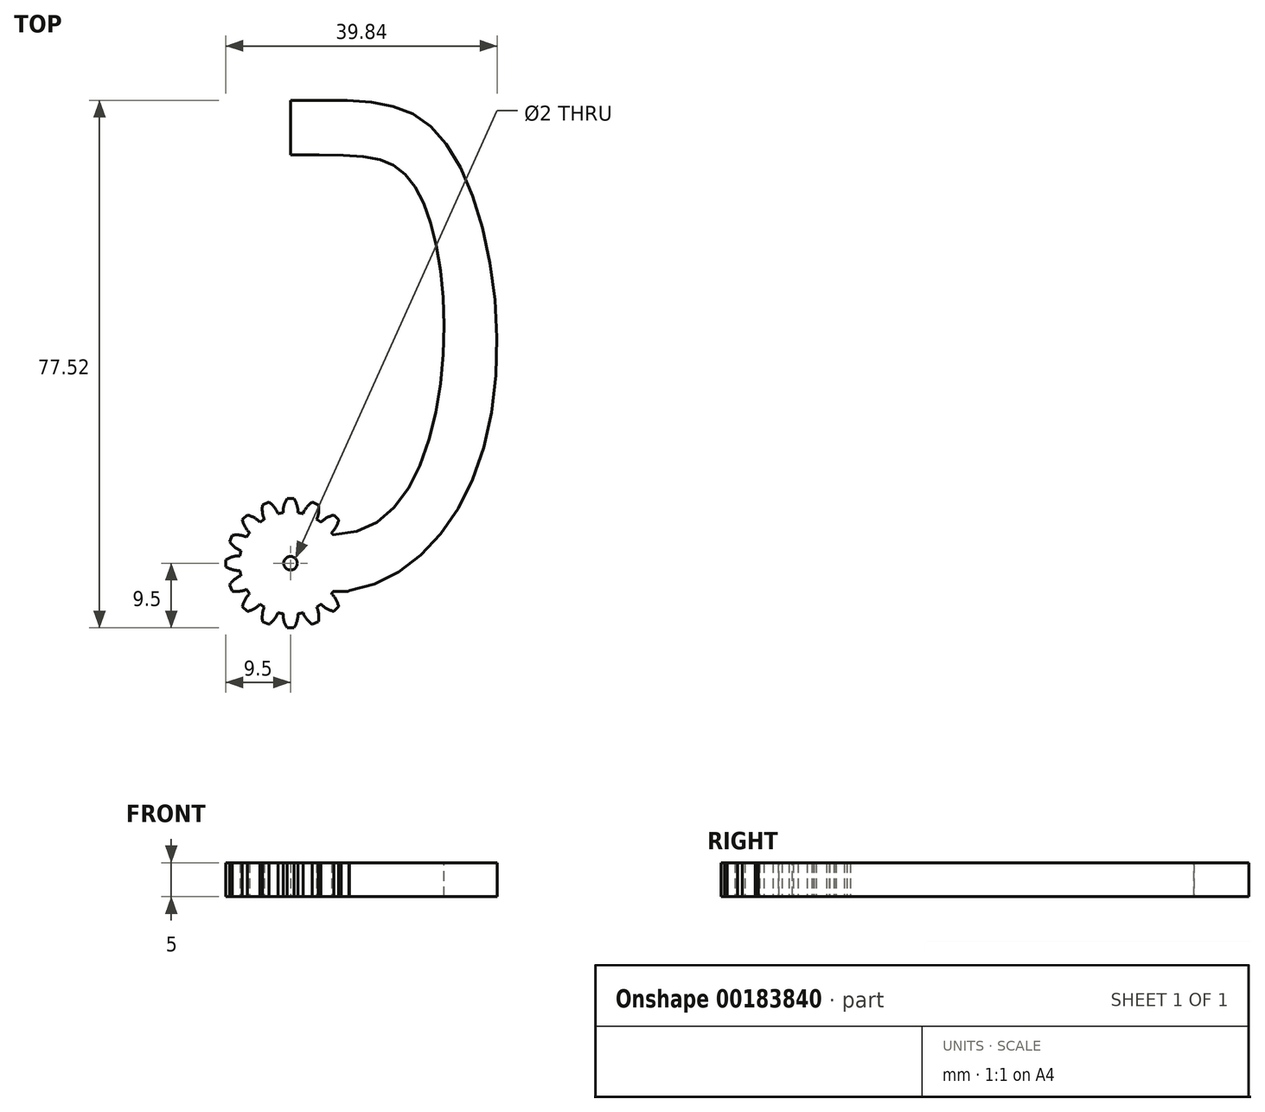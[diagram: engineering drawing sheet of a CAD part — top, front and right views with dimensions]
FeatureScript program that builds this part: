
annotation { "Feature Type Name" : "Feature", "Feature Type Description" : "" }
export const myFeature = defineFeature(function(context is Context, id is Id, definition is map)
    precondition{}
    {
        {
            var Q0;
            Q0=qCreatedBy(makeId("Top.planeOp"),FACE);
            var sketch = newSketch(context, id + "F0", { "sketchPlane" : qUnion([Q0])});
            skCircle(sketch, "E0", {"center": v(0, 0) * mm, "radius": 7.5 * mm});
            skLineSegment(sketch, "E1", {"start": v(0, 0) * mm, "end": v(0, 7.5) * mm, "construction": true});
            skLineSegment(sketch, "E2", {"start": v(0, 9.5) * mm, "end": v(-0.5, 9.5) * mm});
            skArc(sketch, "E3", {"start": v(-0.5, 9.5) * mm, "mid": v(-0.95, 8.5) * mm, "end": v(-1.09, 7.42) * mm});
            skLineSegment(sketch, "E4.MirrorCS", {"start": v(0, 9.5) * mm, "end": v(0.5, 9.5) * mm});
            skArc(sketch, "E5.MirrorCS", {"start": v(0.5, 9.5) * mm, "mid": v(0.95, 8.5) * mm, "end": v(1.09, 7.42) * mm});
            skArc(sketch, "E6.1.0", {"start": v(-4.1, 8.59) * mm, "mid": v(-4.13, 7.5) * mm, "end": v(-3.85, 6.44) * mm});
            skLineSegment(sketch, "E6.1.1", {"start": v(-3.64, 8.78) * mm, "end": v(-4.1, 8.59) * mm});
            skLineSegment(sketch, "E6.1.2", {"start": v(-3.64, 8.78) * mm, "end": v(-3.17, 8.97) * mm});
            skArc(sketch, "E6.1.3", {"start": v(-3.17, 8.97) * mm, "mid": v(-2.38, 8.22) * mm, "end": v(-1.83, 7.27) * mm});
            skArc(sketch, "E6.2.0", {"start": v(-7.07, 6.36) * mm, "mid": v(-6.69, 5.34) * mm, "end": v(-6.02, 4.48) * mm});
            skLineSegment(sketch, "E6.2.1", {"start": v(-6.72, 6.72) * mm, "end": v(-7.07, 6.36) * mm});
            skLineSegment(sketch, "E6.2.2", {"start": v(-6.72, 6.72) * mm, "end": v(-6.36, 7.07) * mm});
            skArc(sketch, "E6.2.3", {"start": v(-6.36, 7.07) * mm, "mid": v(-5.34, 6.69) * mm, "end": v(-4.48, 6.02) * mm});
            skArc(sketch, "E6.3.0", {"start": v(-8.97, 3.17) * mm, "mid": v(-8.22, 2.38) * mm, "end": v(-7.27, 1.83) * mm});
            skLineSegment(sketch, "E6.3.1", {"start": v(-8.78, 3.64) * mm, "end": v(-8.97, 3.17) * mm});
            skLineSegment(sketch, "E6.3.2", {"start": v(-8.78, 3.64) * mm, "end": v(-8.59, 4.1) * mm});
            skArc(sketch, "E6.3.3", {"start": v(-8.59, 4.1) * mm, "mid": v(-7.5, 4.13) * mm, "end": v(-6.44, 3.85) * mm});
            skArc(sketch, "E6.4.0", {"start": v(-9.5, -0.5) * mm, "mid": v(-8.5, -0.95) * mm, "end": v(-7.42, -1.09) * mm});
            skLineSegment(sketch, "E6.4.1", {"start": v(-9.5, 0) * mm, "end": v(-9.5, -0.5) * mm});
            skLineSegment(sketch, "E6.4.2", {"start": v(-9.5, 0) * mm, "end": v(-9.5, 0.5) * mm});
            skArc(sketch, "E6.4.3", {"start": v(-9.5, 0.5) * mm, "mid": v(-8.5, 0.95) * mm, "end": v(-7.42, 1.09) * mm});
            skArc(sketch, "E6.5.0", {"start": v(-8.59, -4.1) * mm, "mid": v(-7.5, -4.13) * mm, "end": v(-6.44, -3.85) * mm});
            skLineSegment(sketch, "E6.5.1", {"start": v(-8.78, -3.64) * mm, "end": v(-8.59, -4.1) * mm});
            skLineSegment(sketch, "E6.5.2", {"start": v(-8.78, -3.64) * mm, "end": v(-8.97, -3.17) * mm});
            skArc(sketch, "E6.5.3", {"start": v(-8.97, -3.17) * mm, "mid": v(-8.22, -2.38) * mm, "end": v(-7.27, -1.83) * mm});
            skArc(sketch, "E6.6.0", {"start": v(-6.36, -7.07) * mm, "mid": v(-5.34, -6.69) * mm, "end": v(-4.48, -6.02) * mm});
            skLineSegment(sketch, "E6.6.1", {"start": v(-6.72, -6.72) * mm, "end": v(-6.36, -7.07) * mm});
            skLineSegment(sketch, "E6.6.2", {"start": v(-6.72, -6.72) * mm, "end": v(-7.07, -6.36) * mm});
            skArc(sketch, "E6.6.3", {"start": v(-7.07, -6.36) * mm, "mid": v(-6.69, -5.34) * mm, "end": v(-6.02, -4.48) * mm});
            skArc(sketch, "E6.7.0", {"start": v(-3.17, -8.97) * mm, "mid": v(-2.38, -8.22) * mm, "end": v(-1.83, -7.27) * mm});
            skLineSegment(sketch, "E6.7.1", {"start": v(-3.64, -8.78) * mm, "end": v(-3.17, -8.97) * mm});
            skLineSegment(sketch, "E6.7.2", {"start": v(-3.64, -8.78) * mm, "end": v(-4.1, -8.59) * mm});
            skArc(sketch, "E6.7.3", {"start": v(-4.1, -8.59) * mm, "mid": v(-4.13, -7.5) * mm, "end": v(-3.85, -6.44) * mm});
            skArc(sketch, "E6.8.0", {"start": v(0.5, -9.5) * mm, "mid": v(0.95, -8.5) * mm, "end": v(1.09, -7.42) * mm});
            skLineSegment(sketch, "E6.8.1", {"start": v(0, -9.5) * mm, "end": v(0.5, -9.5) * mm});
            skLineSegment(sketch, "E6.8.2", {"start": v(0, -9.5) * mm, "end": v(-0.5, -9.5) * mm});
            skArc(sketch, "E6.8.3", {"start": v(-0.5, -9.5) * mm, "mid": v(-0.95, -8.5) * mm, "end": v(-1.09, -7.42) * mm});
            skArc(sketch, "E6.9.0", {"start": v(4.1, -8.59) * mm, "mid": v(4.13, -7.5) * mm, "end": v(3.85, -6.44) * mm});
            skLineSegment(sketch, "E6.9.1", {"start": v(3.64, -8.78) * mm, "end": v(4.1, -8.59) * mm});
            skLineSegment(sketch, "E6.9.2", {"start": v(3.64, -8.78) * mm, "end": v(3.17, -8.97) * mm});
            skArc(sketch, "E6.9.3", {"start": v(3.17, -8.97) * mm, "mid": v(2.38, -8.22) * mm, "end": v(1.83, -7.27) * mm});
            skArc(sketch, "E6.10.0", {"start": v(7.07, -6.36) * mm, "mid": v(6.69, -5.34) * mm, "end": v(6.02, -4.48) * mm});
            skLineSegment(sketch, "E6.10.1", {"start": v(6.72, -6.72) * mm, "end": v(7.07, -6.36) * mm});
            skLineSegment(sketch, "E6.10.2", {"start": v(6.72, -6.72) * mm, "end": v(6.36, -7.07) * mm});
            skArc(sketch, "E6.10.3", {"start": v(6.36, -7.07) * mm, "mid": v(5.34, -6.69) * mm, "end": v(4.48, -6.02) * mm});
            skArc(sketch, "E6.11.0", {"start": v(8.97, -3.17) * mm, "mid": v(8.22, -2.38) * mm, "end": v(7.27, -1.83) * mm});
            skLineSegment(sketch, "E6.11.1", {"start": v(8.78, -3.64) * mm, "end": v(8.97, -3.17) * mm});
            skLineSegment(sketch, "E6.11.2", {"start": v(8.78, -3.64) * mm, "end": v(8.59, -4.1) * mm});
            skArc(sketch, "E6.11.3", {"start": v(8.59, -4.1) * mm, "mid": v(7.5, -4.13) * mm, "end": v(6.44, -3.85) * mm});
            skArc(sketch, "E6.12.0", {"start": v(9.5, 0.5) * mm, "mid": v(8.5, 0.95) * mm, "end": v(7.42, 1.09) * mm});
            skLineSegment(sketch, "E6.12.1", {"start": v(9.5, 0) * mm, "end": v(9.5, 0.5) * mm});
            skLineSegment(sketch, "E6.12.2", {"start": v(9.5, 0) * mm, "end": v(9.5, -0.5) * mm});
            skArc(sketch, "E6.12.3", {"start": v(9.5, -0.5) * mm, "mid": v(8.5, -0.95) * mm, "end": v(7.42, -1.09) * mm});
            skArc(sketch, "E6.13.0", {"start": v(8.59, 4.1) * mm, "mid": v(7.5, 4.13) * mm, "end": v(6.44, 3.85) * mm});
            skLineSegment(sketch, "E6.13.1", {"start": v(8.78, 3.64) * mm, "end": v(8.59, 4.1) * mm});
            skLineSegment(sketch, "E6.13.2", {"start": v(8.78, 3.64) * mm, "end": v(8.97, 3.17) * mm});
            skArc(sketch, "E6.13.3", {"start": v(8.97, 3.17) * mm, "mid": v(8.22, 2.38) * mm, "end": v(7.27, 1.83) * mm});
            skArc(sketch, "E6.14.0", {"start": v(6.36, 7.07) * mm, "mid": v(5.34, 6.69) * mm, "end": v(4.48, 6.02) * mm});
            skLineSegment(sketch, "E6.14.1", {"start": v(6.72, 6.72) * mm, "end": v(6.36, 7.07) * mm});
            skLineSegment(sketch, "E6.14.2", {"start": v(6.72, 6.72) * mm, "end": v(7.07, 6.36) * mm});
            skArc(sketch, "E6.14.3", {"start": v(7.07, 6.36) * mm, "mid": v(6.69, 5.34) * mm, "end": v(6.02, 4.48) * mm});
            skArc(sketch, "E6.15.0", {"start": v(3.17, 8.97) * mm, "mid": v(2.38, 8.22) * mm, "end": v(1.83, 7.27) * mm});
            skLineSegment(sketch, "E6.15.1", {"start": v(3.64, 8.78) * mm, "end": v(3.17, 8.97) * mm});
            skLineSegment(sketch, "E6.15.2", {"start": v(3.64, 8.78) * mm, "end": v(4.1, 8.59) * mm});
            skArc(sketch, "E6.15.3", {"start": v(4.1, 8.59) * mm, "mid": v(4.13, 7.5) * mm, "end": v(3.85, 6.44) * mm});
            skSolve(sketch);
        }
        {
            var Q0;
            Q0=qSketchRegion(id+"F0",true);
            extrude(context, id + "F1", {"entities" : qUnion([Q0]), "depth" : 5 * mm});
        }
        {
            var Q0;
            Q0=makeQuery(id+"F1.opExtrude","CAP_FACE",FACE,{"disambiguationData":[OSD([sQuery(id+"F0.wireOp",EDGE,"E0"),sQuery(id+"F0.wireOp",EDGE,"E2"),sQuery(id+"F0.wireOp",EDGE,"E3"),sQuery(id+"F0.wireOp",EDGE,"E4.MirrorCS"),sQuery(id+"F0.wireOp",EDGE,"E5.MirrorCS"),sQuery(id+"F0.wireOp",EDGE,"E6.1.0"),sQuery(id+"F0.wireOp",EDGE,"E6.1.1"),sQuery(id+"F0.wireOp",EDGE,"E6.1.2"),sQuery(id+"F0.wireOp",EDGE,"E6.1.3"),sQuery(id+"F0.wireOp",EDGE,"E6.2.0"),sQuery(id+"F0.wireOp",EDGE,"E6.2.1"),sQuery(id+"F0.wireOp",EDGE,"E6.2.2"),sQuery(id+"F0.wireOp",EDGE,"E6.2.3"),sQuery(id+"F0.wireOp",EDGE,"E6.3.0"),sQuery(id+"F0.wireOp",EDGE,"E6.3.1"),sQuery(id+"F0.wireOp",EDGE,"E6.3.2"),sQuery(id+"F0.wireOp",EDGE,"E6.3.3"),sQuery(id+"F0.wireOp",EDGE,"E6.4.0"),sQuery(id+"F0.wireOp",EDGE,"E6.4.1"),sQuery(id+"F0.wireOp",EDGE,"E6.4.2"),sQuery(id+"F0.wireOp",EDGE,"E6.4.3"),sQuery(id+"F0.wireOp",EDGE,"E6.5.0"),sQuery(id+"F0.wireOp",EDGE,"E6.5.1"),sQuery(id+"F0.wireOp",EDGE,"E6.5.2"),sQuery(id+"F0.wireOp",EDGE,"E6.5.3"),sQuery(id+"F0.wireOp",EDGE,"E6.6.0"),sQuery(id+"F0.wireOp",EDGE,"E6.6.1"),sQuery(id+"F0.wireOp",EDGE,"E6.6.2"),sQuery(id+"F0.wireOp",EDGE,"E6.6.3"),sQuery(id+"F0.wireOp",EDGE,"E6.7.0"),sQuery(id+"F0.wireOp",EDGE,"E6.7.1"),sQuery(id+"F0.wireOp",EDGE,"E6.7.2"),sQuery(id+"F0.wireOp",EDGE,"E6.7.3"),sQuery(id+"F0.wireOp",EDGE,"E6.8.0"),sQuery(id+"F0.wireOp",EDGE,"E6.8.1"),sQuery(id+"F0.wireOp",EDGE,"E6.8.2"),sQuery(id+"F0.wireOp",EDGE,"E6.8.3"),sQuery(id+"F0.wireOp",EDGE,"E6.9.0"),sQuery(id+"F0.wireOp",EDGE,"E6.9.1"),sQuery(id+"F0.wireOp",EDGE,"E6.9.2"),sQuery(id+"F0.wireOp",EDGE,"E6.9.3"),sQuery(id+"F0.wireOp",EDGE,"E6.10.0"),sQuery(id+"F0.wireOp",EDGE,"E6.10.1"),sQuery(id+"F0.wireOp",EDGE,"E6.10.2"),sQuery(id+"F0.wireOp",EDGE,"E6.10.3"),sQuery(id+"F0.wireOp",EDGE,"E6.11.0"),sQuery(id+"F0.wireOp",EDGE,"E6.11.1"),sQuery(id+"F0.wireOp",EDGE,"E6.11.2"),sQuery(id+"F0.wireOp",EDGE,"E6.11.3"),sQuery(id+"F0.wireOp",EDGE,"E6.12.0"),sQuery(id+"F0.wireOp",EDGE,"E6.12.1"),sQuery(id+"F0.wireOp",EDGE,"E6.12.2"),sQuery(id+"F0.wireOp",EDGE,"E6.12.3"),sQuery(id+"F0.wireOp",EDGE,"E6.13.0"),sQuery(id+"F0.wireOp",EDGE,"E6.13.1"),sQuery(id+"F0.wireOp",EDGE,"E6.13.2"),sQuery(id+"F0.wireOp",EDGE,"E6.13.3"),sQuery(id+"F0.wireOp",EDGE,"E6.14.0"),sQuery(id+"F0.wireOp",EDGE,"E6.14.1"),sQuery(id+"F0.wireOp",EDGE,"E6.14.2"),sQuery(id+"F0.wireOp",EDGE,"E6.14.3"),sQuery(id+"F0.wireOp",EDGE,"E6.15.0"),sQuery(id+"F0.wireOp",EDGE,"E6.15.1"),sQuery(id+"F0.wireOp",EDGE,"E6.15.2"),sQuery(id+"F0.wireOp",EDGE,"E6.15.3")])],"isStart":false});
            var sketch = newSketch(context, id + "F2", { "sketchPlane" : qUnion([Q0])});
            skCircle(sketch, "E7", {"center": v(0, 0) * mm, "radius": 1 * mm});
            skSolve(sketch);
        }
        {
            var Q0;
            Q0=makeQuery(id+"F2.imprint","IMPRINT",FACE,{"disambiguationData":[TD([[makeQuery(id+"F2.imprint","IMPRINT",EDGE,{"derivedFrom":sQuery(id+"F2.wireOp",EDGE,"E7")}),1.0]])]});
            extrude(context, id + "F3", {"entities" : qUnion([Q0]), "operationType" : NewBodyOperationType.REMOVE, "endBound" : BoundingType.THROUGH_ALL, "oppositeDirection" : true, "depth" : 13.9 * mm});
        }
        {
            var Q0;
            Q0=qCreatedBy(makeId("Top.planeOp"),FACE);
            var sketch = newSketch(context, id + "F4", { "sketchPlane" : qUnion([Q0])});
            skLineSegment(sketch, "E8", {"start": v(0, 68) * mm, "end": v(0, 60) * mm});
            skFitSpline(sketch, "E9", {"points": [v(0, 60) * mm, v(17.62, 56.25) * mm, v(22.06, 26.65) * mm, v(6.24, 4.17) * mm], "startDerivative": vector(105.74, 0) * mm, "endDerivative": vector(-85.58, 0) * mm});
            skFitSpline(sketch, "E10", {"points": [v(0, 68) * mm, v(21.87, 62.86) * mm, v(28.54, 17.44) * mm, v(6.24, -4.17) * mm], "startDerivative": vector(108.16, 0) * mm, "endDerivative": vector(-91.99, 0) * mm});
            skLineSegment(sketch, "E11", {"start": v(6.24, 4.17) * mm, "end": v(6.24, -4.17) * mm});
            skSolve(sketch);
        }
        {
            var Q0;
            Q0 = qSketchRegion(id + "F4", true);
            var Q1;
            Q1=makeQuery(id+"F1.opExtrude","CAP_FACE",FACE,{"disambiguationData":[OSD([sQuery(id+"F0.wireOp",EDGE,"E0"),sQuery(id+"F0.wireOp",EDGE,"E2"),sQuery(id+"F0.wireOp",EDGE,"E3"),sQuery(id+"F0.wireOp",EDGE,"E4.MirrorCS"),sQuery(id+"F0.wireOp",EDGE,"E5.MirrorCS"),sQuery(id+"F0.wireOp",EDGE,"E6.1.0"),sQuery(id+"F0.wireOp",EDGE,"E6.1.1"),sQuery(id+"F0.wireOp",EDGE,"E6.1.2"),sQuery(id+"F0.wireOp",EDGE,"E6.1.3"),sQuery(id+"F0.wireOp",EDGE,"E6.2.0"),sQuery(id+"F0.wireOp",EDGE,"E6.2.1"),sQuery(id+"F0.wireOp",EDGE,"E6.2.2"),sQuery(id+"F0.wireOp",EDGE,"E6.2.3"),sQuery(id+"F0.wireOp",EDGE,"E6.3.0"),sQuery(id+"F0.wireOp",EDGE,"E6.3.1"),sQuery(id+"F0.wireOp",EDGE,"E6.3.2"),sQuery(id+"F0.wireOp",EDGE,"E6.3.3"),sQuery(id+"F0.wireOp",EDGE,"E6.4.0"),sQuery(id+"F0.wireOp",EDGE,"E6.4.1"),sQuery(id+"F0.wireOp",EDGE,"E6.4.2"),sQuery(id+"F0.wireOp",EDGE,"E6.4.3"),sQuery(id+"F0.wireOp",EDGE,"E6.5.0"),sQuery(id+"F0.wireOp",EDGE,"E6.5.1"),sQuery(id+"F0.wireOp",EDGE,"E6.5.2"),sQuery(id+"F0.wireOp",EDGE,"E6.5.3"),sQuery(id+"F0.wireOp",EDGE,"E6.6.0"),sQuery(id+"F0.wireOp",EDGE,"E6.6.1"),sQuery(id+"F0.wireOp",EDGE,"E6.6.2"),sQuery(id+"F0.wireOp",EDGE,"E6.6.3"),sQuery(id+"F0.wireOp",EDGE,"E6.7.0"),sQuery(id+"F0.wireOp",EDGE,"E6.7.1"),sQuery(id+"F0.wireOp",EDGE,"E6.7.2"),sQuery(id+"F0.wireOp",EDGE,"E6.7.3"),sQuery(id+"F0.wireOp",EDGE,"E6.8.0"),sQuery(id+"F0.wireOp",EDGE,"E6.8.1"),sQuery(id+"F0.wireOp",EDGE,"E6.8.2"),sQuery(id+"F0.wireOp",EDGE,"E6.8.3"),sQuery(id+"F0.wireOp",EDGE,"E6.9.0"),sQuery(id+"F0.wireOp",EDGE,"E6.9.1"),sQuery(id+"F0.wireOp",EDGE,"E6.9.2"),sQuery(id+"F0.wireOp",EDGE,"E6.9.3"),sQuery(id+"F0.wireOp",EDGE,"E6.10.0"),sQuery(id+"F0.wireOp",EDGE,"E6.10.1"),sQuery(id+"F0.wireOp",EDGE,"E6.10.2"),sQuery(id+"F0.wireOp",EDGE,"E6.10.3"),sQuery(id+"F0.wireOp",EDGE,"E6.11.0"),sQuery(id+"F0.wireOp",EDGE,"E6.11.1"),sQuery(id+"F0.wireOp",EDGE,"E6.11.2"),sQuery(id+"F0.wireOp",EDGE,"E6.11.3"),sQuery(id+"F0.wireOp",EDGE,"E6.12.0"),sQuery(id+"F0.wireOp",EDGE,"E6.12.1"),sQuery(id+"F0.wireOp",EDGE,"E6.12.2"),sQuery(id+"F0.wireOp",EDGE,"E6.12.3"),sQuery(id+"F0.wireOp",EDGE,"E6.13.0"),sQuery(id+"F0.wireOp",EDGE,"E6.13.1"),sQuery(id+"F0.wireOp",EDGE,"E6.13.2"),sQuery(id+"F0.wireOp",EDGE,"E6.13.3"),sQuery(id+"F0.wireOp",EDGE,"E6.14.0"),sQuery(id+"F0.wireOp",EDGE,"E6.14.1"),sQuery(id+"F0.wireOp",EDGE,"E6.14.2"),sQuery(id+"F0.wireOp",EDGE,"E6.14.3"),sQuery(id+"F0.wireOp",EDGE,"E6.15.0"),sQuery(id+"F0.wireOp",EDGE,"E6.15.1"),sQuery(id+"F0.wireOp",EDGE,"E6.15.2"),sQuery(id+"F0.wireOp",EDGE,"E6.15.3")])],"isStart":false});
            extrude(context, id + "F5", {"entities" : qUnion([Q0]), "operationType" : NewBodyOperationType.ADD, "endBound" : BoundingType.UP_TO_SURFACE, "endBoundEntityFace" : qUnion([Q1]), "depth" : 25 * mm});
        }
    });
